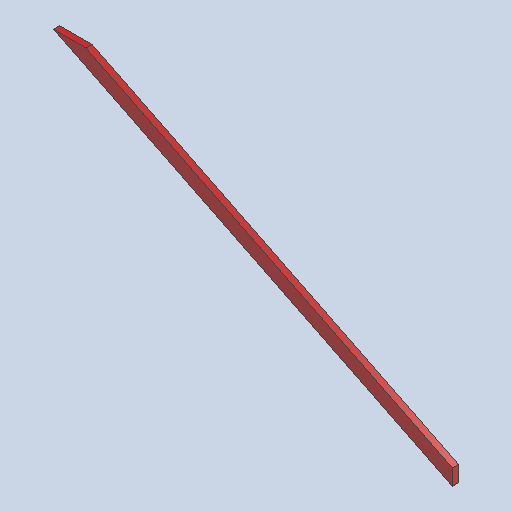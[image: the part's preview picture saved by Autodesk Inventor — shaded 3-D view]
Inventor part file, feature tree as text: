
AUTODESK INVENTOR PART (.ipt)
format: ipt  version: 2025.1 (Build 291241020, 241B)  size: 253,952 bytes
history: native  units: in
note: dims shown in document units (in); Inventor stores cm internally (conversion verified against a paired STEP export)
features: other x6, reference x3, extrude x1, sketch x1
ambient origin geometry x8: Origin, YZ Plane, XZ Plane, XY Plane, X Axis, Y Axis, Z Axis, Center Point
bodies: Solid1 (feature_tree)
feature tree (11):
  extrude  "Extrusion1"  Depth=1.5in TaperAngle=0.0deg
  sketch  "Sketch1"  dims[d0=3.5in d1=1.5in d2=0.0in]
  reference  "Reference1"
  reference  "Reference2"
  reference  "Reference3"
  other  "<userpath>\Documents\Tburn24\layer2\layer2.iam"
  other  "layer2.iam"
  other  "8'x2x4:3"
  other  "12'x2x4:1"
  other  "8'x2x4:6"
  other  "Finish1"
